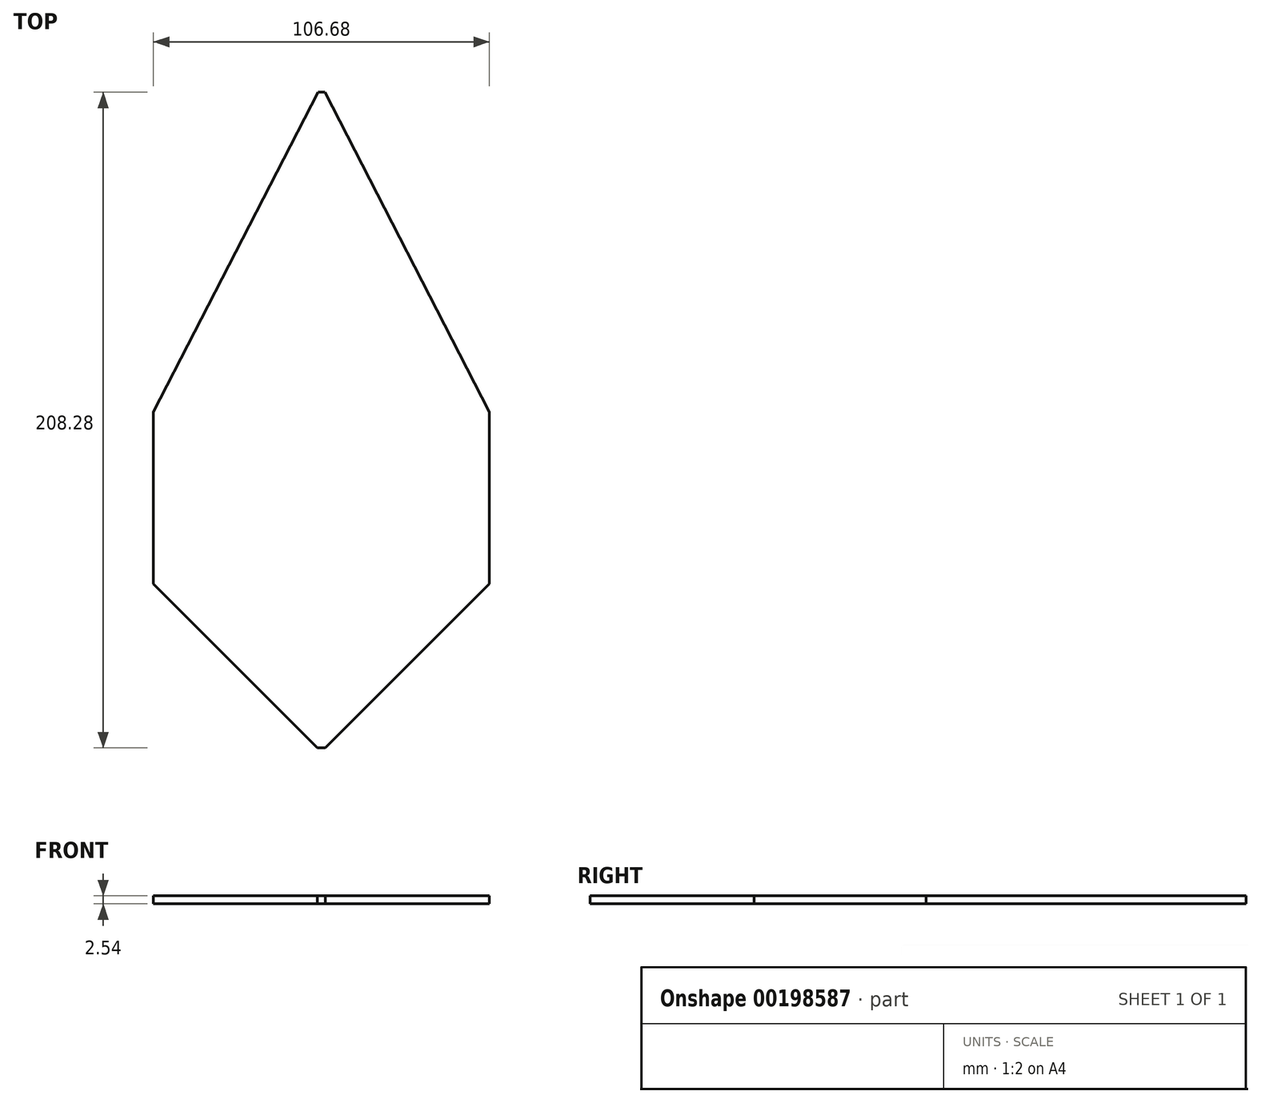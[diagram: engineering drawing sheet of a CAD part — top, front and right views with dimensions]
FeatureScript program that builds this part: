
annotation { "Feature Type Name" : "Feature", "Feature Type Description" : "" }
export const myFeature = defineFeature(function(context is Context, id is Id, definition is map)
    precondition{}
    {
        {
            var Q0;
            Q0=qCreatedBy(makeId("Top.planeOp"),FACE);
            var sketch = newSketch(context, id + "F0", { "sketchPlane" : qUnion([Q0])});
            skLineSegment(sketch, "E0.bottom", {"start": v(53.34, 104.14) * mm, "end": v(-53.34, 104.14) * mm});
            skLineSegment(sketch, "E0.top", {"start": v(53.34, -104.14) * mm, "end": v(-53.34, -104.14) * mm});
            skLineSegment(sketch, "E0.left", {"start": v(53.34, 104.14) * mm, "end": v(53.34, -104.14) * mm});
            skLineSegment(sketch, "E0.right", {"start": v(-53.34, 104.14) * mm, "end": v(-53.34, -104.14) * mm});
            skPoint(sketch, "E0.middle", {"position": v(0, 0) * mm});
            skSolve(sketch);
        }
        {
            var Q0;
            Q0=makeQuery(id+"F0.imprint","IMPRINT",FACE,{"disambiguationData":[TD([[makeQuery(id+"F0.imprint","IMPRINT",EDGE,{"derivedFrom":sQuery(id+"F0.wireOp",EDGE,"E0.bottom")}),1.0]])]});
            extrude(context, id + "F1", {"entities" : qUnion([Q0]), "depth" : 2.54 * mm});
        }
        {
            var Q0;
            Q0=makeQuery(id+"F1.opExtrude","SWEPT_EDGE",EDGE,{"disambiguationData":[OSD([sQuery(id+"F0.wireOp",EDGE,"E0.top"),sQuery(id+"F0.wireOp",EDGE,"E0.right")])]});
            var Q1;
            Q1=makeQuery(id+"F1.opExtrude","SWEPT_EDGE",EDGE,{"disambiguationData":[OSD([sQuery(id+"F0.wireOp",EDGE,"E0.top"),sQuery(id+"F0.wireOp",EDGE,"E0.left")])]});
            chamfer(context, id + "F2", {"entities" : qUnion([Q0, Q1]), "width" : 52.07 * mm, "tangentPropagation" : true});
        }
        {
            var Q0;
            Q0=makeQuery(id+"F1.opExtrude","SWEPT_EDGE",EDGE,{"disambiguationData":[OSD([sQuery(id+"F0.wireOp",EDGE,"E0.bottom"),sQuery(id+"F0.wireOp",EDGE,"E0.right")])]});
            var Q1;
            Q1=makeQuery(id+"F1.opExtrude","SWEPT_EDGE",EDGE,{"disambiguationData":[OSD([sQuery(id+"F0.wireOp",EDGE,"E0.bottom"),sQuery(id+"F0.wireOp",EDGE,"E0.left")])]});
            chamfer(context, id + "F3", {"entities" : qUnion([Q0, Q1]), "chamferType" : ChamferType.OFFSET_ANGLE, "width" : 101.6 * mm, "oppositeDirection" : false, "angle" : 27.2 * degree, "tangentPropagation" : true});
        }
    });
